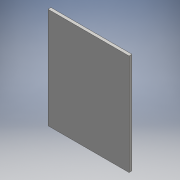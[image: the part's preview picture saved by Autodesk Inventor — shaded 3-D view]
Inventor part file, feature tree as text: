
AUTODESK INVENTOR PART (.ipt)
format: ipt  version: 2016 (Build 200138000, 138)  size: 85,504 bytes
history: native  units: mm
features: other x1, extrude x1, sketch x1
ambient origin geometry x8: Origin, YZ Plane, XZ Plane, XY Plane, X Axis, Y Axis, Z Axis, Center Point
bodies: Body1 (feature_tree)
feature tree (3):
  other  "Bryła1"
  extrude  "Wyciągnięcie proste1"  Depth=68.5mm
  sketch  "Szkic1"
